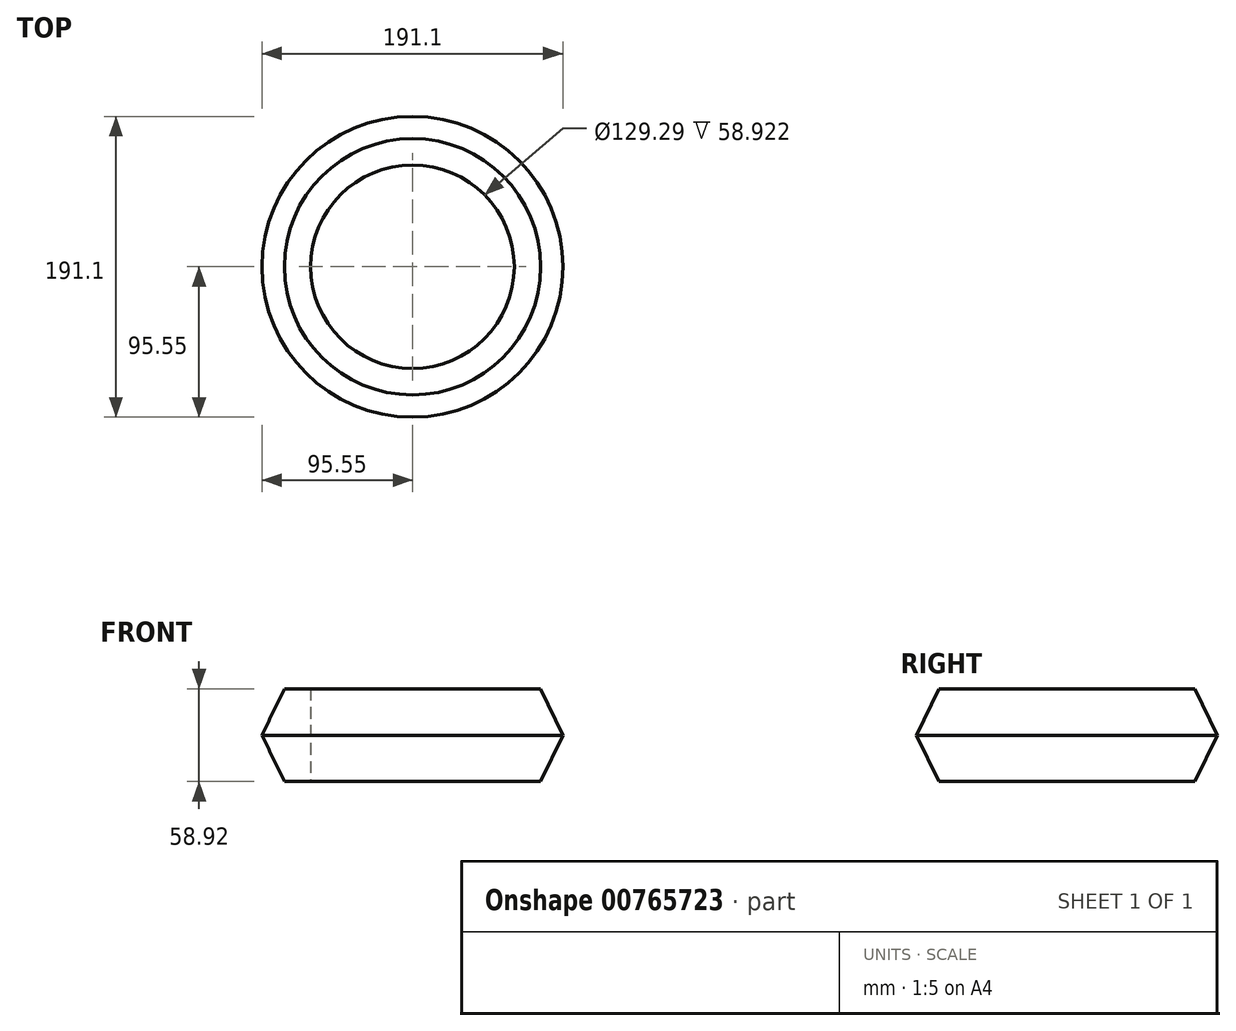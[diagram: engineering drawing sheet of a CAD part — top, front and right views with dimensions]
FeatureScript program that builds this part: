
annotation { "Feature Type Name" : "Feature", "Feature Type Description" : "" }
export const myFeature = defineFeature(function(context is Context, id is Id, definition is map)
    precondition{}
    {
        {
            var Q0;
            Q0=qCreatedBy(makeId("Front.planeOp"),FACE);
            var sketch = newSketch(context, id + "F0", { "sketchPlane" : qUnion([Q0])});
            skLineSegment(sketch, "E0", {"start": v(0, 0) * mm, "end": v(0, 44.16) * mm});
            skLineSegment(sketch, "E1.bottom", {"start": v(81.38, 29.46) * mm, "end": v(64.65, 29.46) * mm});
            skLineSegment(sketch, "E1.top", {"start": v(81.38, -29.46) * mm, "end": v(64.65, -29.46) * mm});
            skLineSegment(sketch, "E1.right", {"start": v(64.65, 29.46) * mm, "end": v(64.65, -29.46) * mm});
            skPoint(sketch, "E1.middle", {"position": v(73.01, 0) * mm});
            skLineSegment(sketch, "E2", {"start": v(81.38, 29.46) * mm, "end": v(95.55, 0) * mm});
            skLineSegment(sketch, "E3", {"start": v(95.55, 0) * mm, "end": v(81.38, -29.46) * mm});
            skSolve(sketch);
        }
        {
            var Q0;
            Q0 = qSketchRegion(id + "F0", true);
            var Q1;
            Q1=sQuery(id+"F0.wireOp",EDGE,"E0");
            revolve(context, id + "F1", {"surfaceOperationType" : NewSurfaceOperationType.NEW, "entities" : qUnion([Q0]), "axis" : qUnion([Q1]), "revolveType" : RevolveType.FULL});
        }
    });
